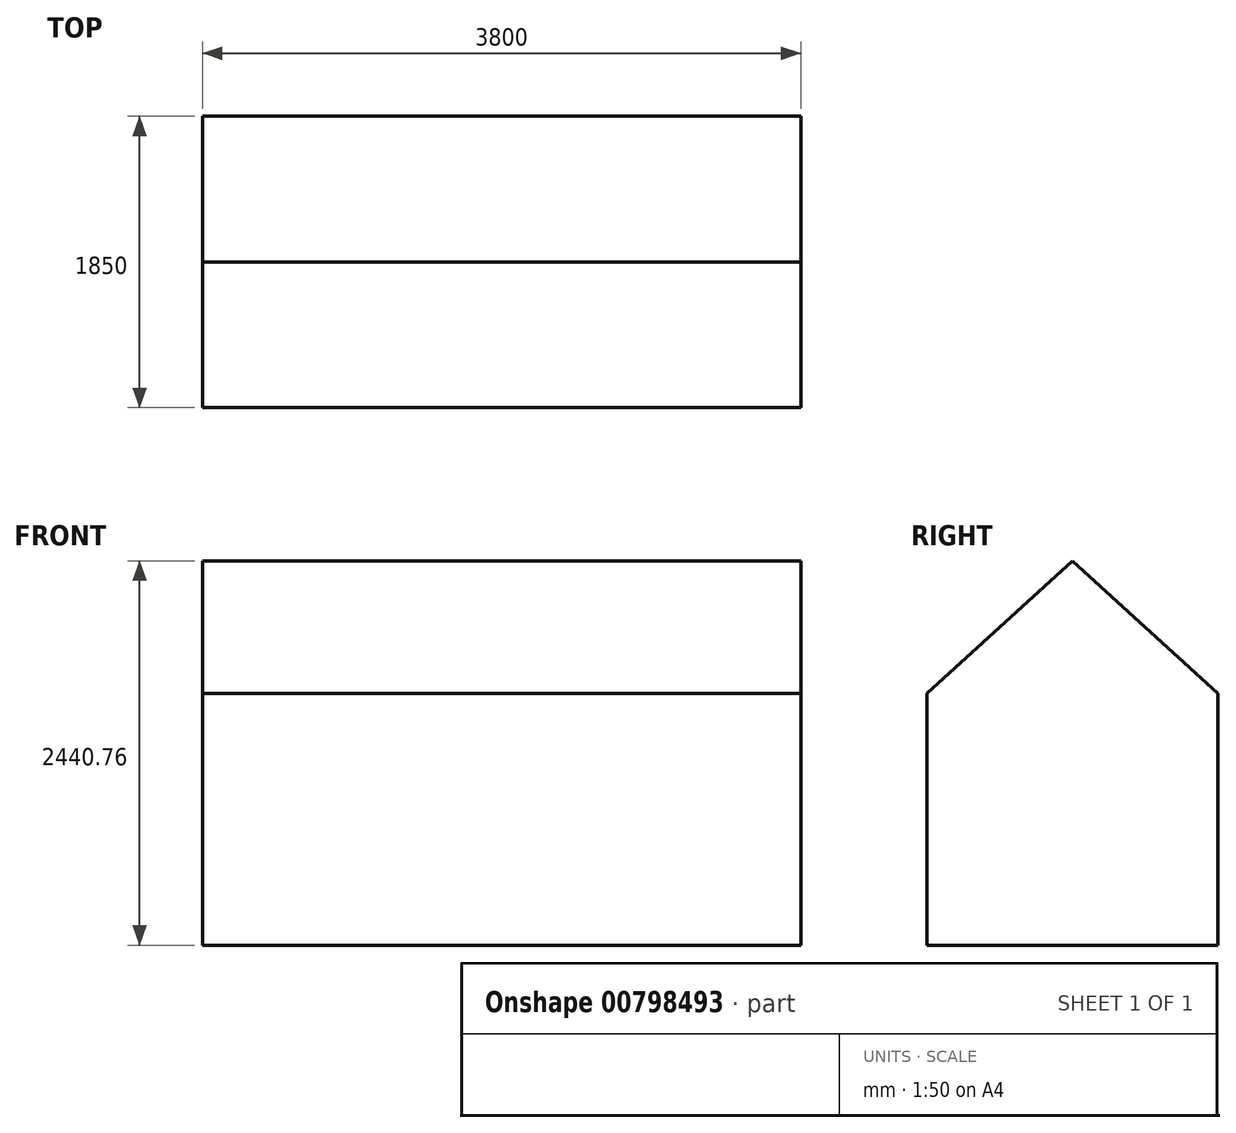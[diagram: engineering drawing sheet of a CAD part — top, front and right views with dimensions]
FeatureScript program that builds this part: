
annotation { "Feature Type Name" : "Feature", "Feature Type Description" : "" }
export const myFeature = defineFeature(function(context is Context, id is Id, definition is map)
    precondition{}
    {
        {
            var Q0;
            Q0=qCreatedBy(makeId("Right.planeOp"),FACE);
            var sketch = newSketch(context, id + "F0", { "sketchPlane" : qUnion([Q0])});
            skLineSegment(sketch, "E0", {"start": v(0, 2440.76) * mm, "end": v(-925, 1600) * mm});
            skLineSegment(sketch, "E1", {"start": v(-925, 1600) * mm, "end": v(-925, 0) * mm});
            skLineSegment(sketch, "E2", {"start": v(-925, 0) * mm, "end": v(925, 0) * mm});
            skLineSegment(sketch, "E3", {"start": v(925, 0) * mm, "end": v(925, 1600) * mm});
            skLineSegment(sketch, "E4", {"start": v(925, 1600) * mm, "end": v(0, 2440.76) * mm});
            skLineSegment(sketch, "E5", {"start": v(-925, 1600) * mm, "end": v(925, 1600) * mm, "construction": true});
            skLineSegment(sketch, "E6", {"start": v(-925, 0) * mm, "end": v(925, 1600) * mm, "construction": true});
            skSolve(sketch);
        }
        {
            var Q0;
            Q0 = qSketchRegion(id + "F0", true);
            extrude(context, id + "F1", {"entities" : qUnion([Q0]), "endBound" : BoundingType.SYMMETRIC, "depth" : 3800 * mm, "offsetDistance" : 25 * mm});
        }
    });
